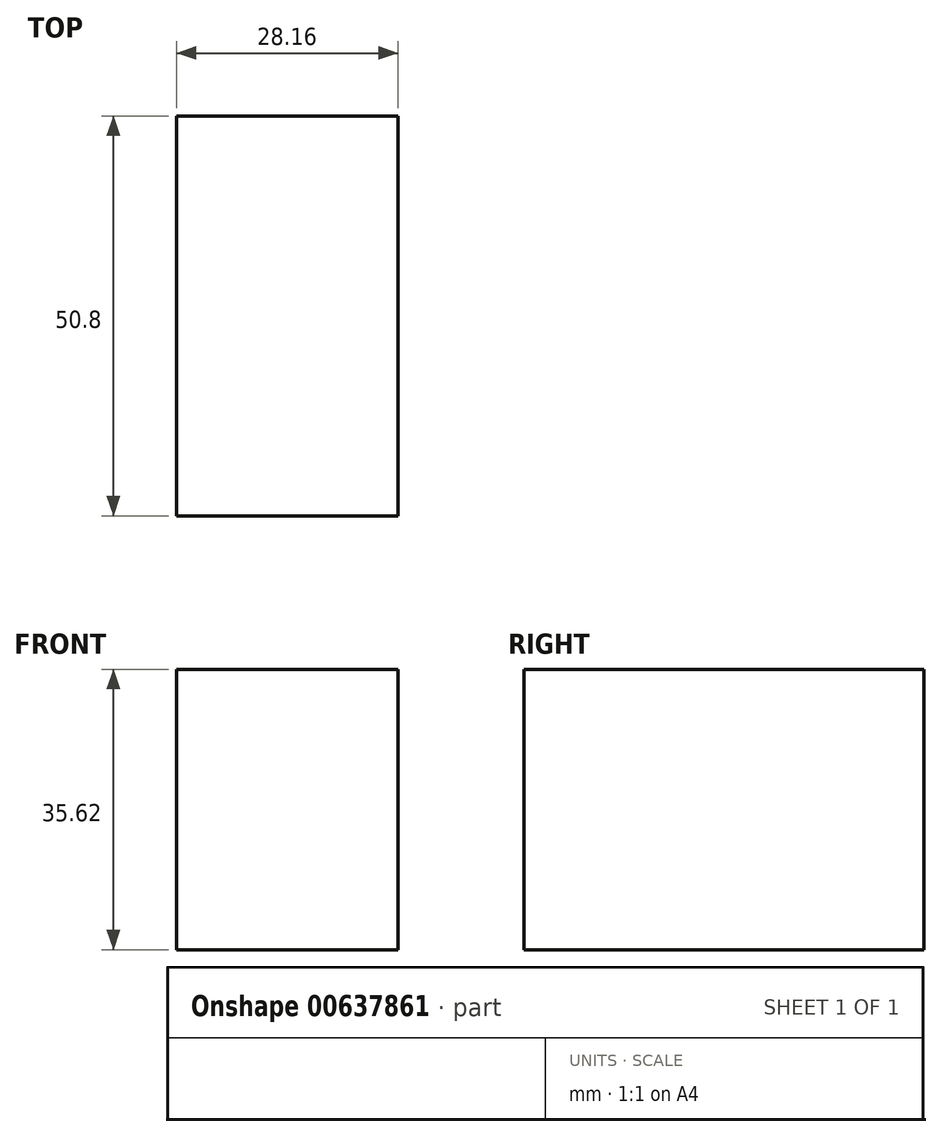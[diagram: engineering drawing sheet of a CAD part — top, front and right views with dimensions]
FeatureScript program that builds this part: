
annotation { "Feature Type Name" : "Feature", "Feature Type Description" : "" }
export const myFeature = defineFeature(function(context is Context, id is Id, definition is map)
    precondition{}
    {
        {
            var Q0;
            Q0=qCreatedBy(makeId("Front.planeOp"),FACE);
            var sketch = newSketch(context, id + "F0", { "sketchPlane" : qUnion([Q0])});
            skLineSegment(sketch, "E0.bottom", {"start": v(-54.73, 56.02) * mm, "end": v(-26.57, 56.02) * mm});
            skLineSegment(sketch, "E0.top", {"start": v(-54.73, 20.4) * mm, "end": v(-26.57, 20.4) * mm});
            skLineSegment(sketch, "E0.left", {"start": v(-54.73, 56.02) * mm, "end": v(-54.73, 20.4) * mm});
            skLineSegment(sketch, "E0.right", {"start": v(-26.57, 56.02) * mm, "end": v(-26.57, 20.4) * mm});
            skSolve(sketch);
        }
        {
            var Q0;
            Q0=makeQuery(id+"F0.imprint","IMPRINT",FACE,{"disambiguationData":[TD([[makeQuery(id+"F0.imprint","IMPRINT",EDGE,{"derivedFrom":sQuery(id+"F0.wireOp",EDGE,"E0.bottom")}),-1.0]])]});
            extrude(context, id + "F1", {"entities" : qUnion([Q0]), "depth" : 50.8 * mm, "offsetDistance" : 25.4 * mm});
        }
    });
